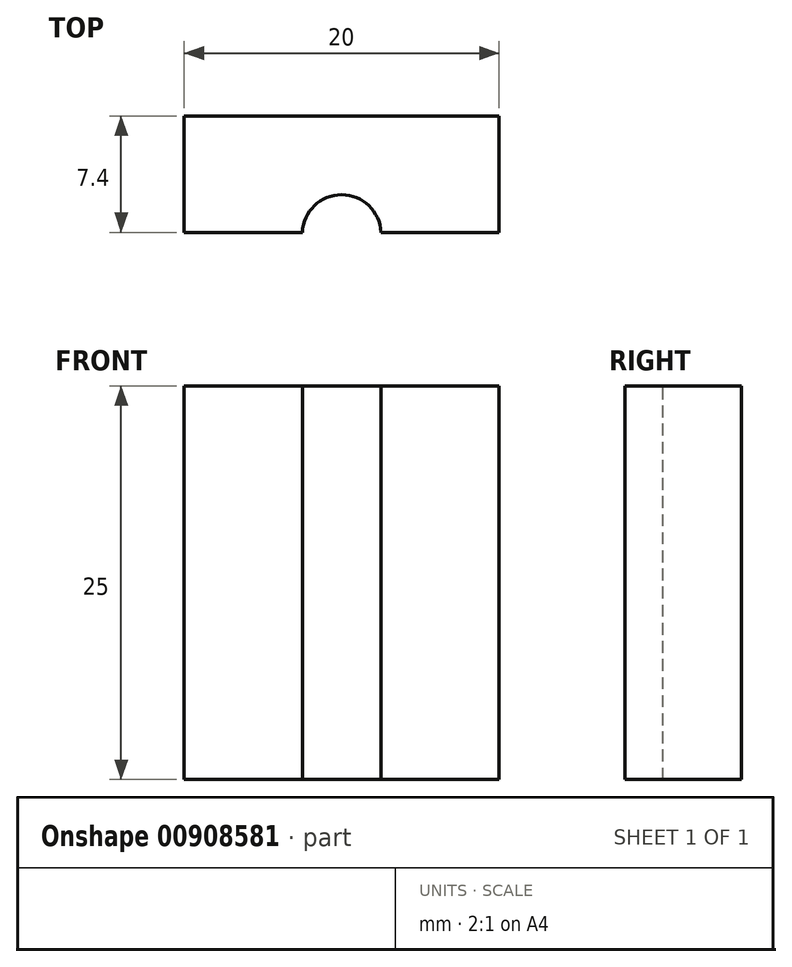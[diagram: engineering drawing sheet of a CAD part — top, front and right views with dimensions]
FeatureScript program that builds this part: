
annotation { "Feature Type Name" : "Feature", "Feature Type Description" : "" }
export const myFeature = defineFeature(function(context is Context, id is Id, definition is map)
    precondition{}
    {
        {
            var Q0;
            Q0=qCreatedBy(makeId("Top.planeOp"),FACE);
            var sketch = newSketch(context, id + "F0", { "sketchPlane" : qUnion([Q0])});
            skLineSegment(sketch, "E0.top", {"start": v(10, 7.5) * mm, "end": v(-10, 7.5) * mm});
            skLineSegment(sketch, "E0.left", {"start": v(10, 0.1) * mm, "end": v(10, 7.5) * mm});
            skPoint(sketch, "E0.middle", {"position": v(0, 0) * mm});
            skArc(sketch, "E1", {"start": v(2.5, 0.1) * mm, "mid": v(0, 2.5) * mm, "end": v(-2.5, 0.1) * mm});
            skLineSegment(sketch, "E2", {"start": v(-10, 0.1) * mm, "end": v(-2.5, 0.1) * mm});
            skLineSegment(sketch, "E3.trimOffspring", {"start": v(2.5, 0.1) * mm, "end": v(10, 0.1) * mm});
            skPoint(sketch, "E4.start.orphan", {"position": v(-10, 0) * mm});
            skPoint(sketch, "E5.trimOffspring.end.orphan", {"position": v(10, 0) * mm});
            skLineSegment(sketch, "E6.trimOffspring", {"start": v(-10, 0.1) * mm, "end": v(-10, 7.5) * mm});
            skPoint(sketch, "E0.bottom.end.orphan", {"position": v(-10, -7.5) * mm});
            skPoint(sketch, "E0.bottom.start.orphan", {"position": v(10, -7.5) * mm});
            skSolve(sketch);
        }
        {
            var Q0;
            Q0 = qSketchRegion(id + "F0", true);
            extrude(context, id + "F1", {"entities" : qUnion([Q0]), "oppositeDirection" : true, "depth" : 25 * mm, "offsetDistance" : 25 * mm});
        }
    });
